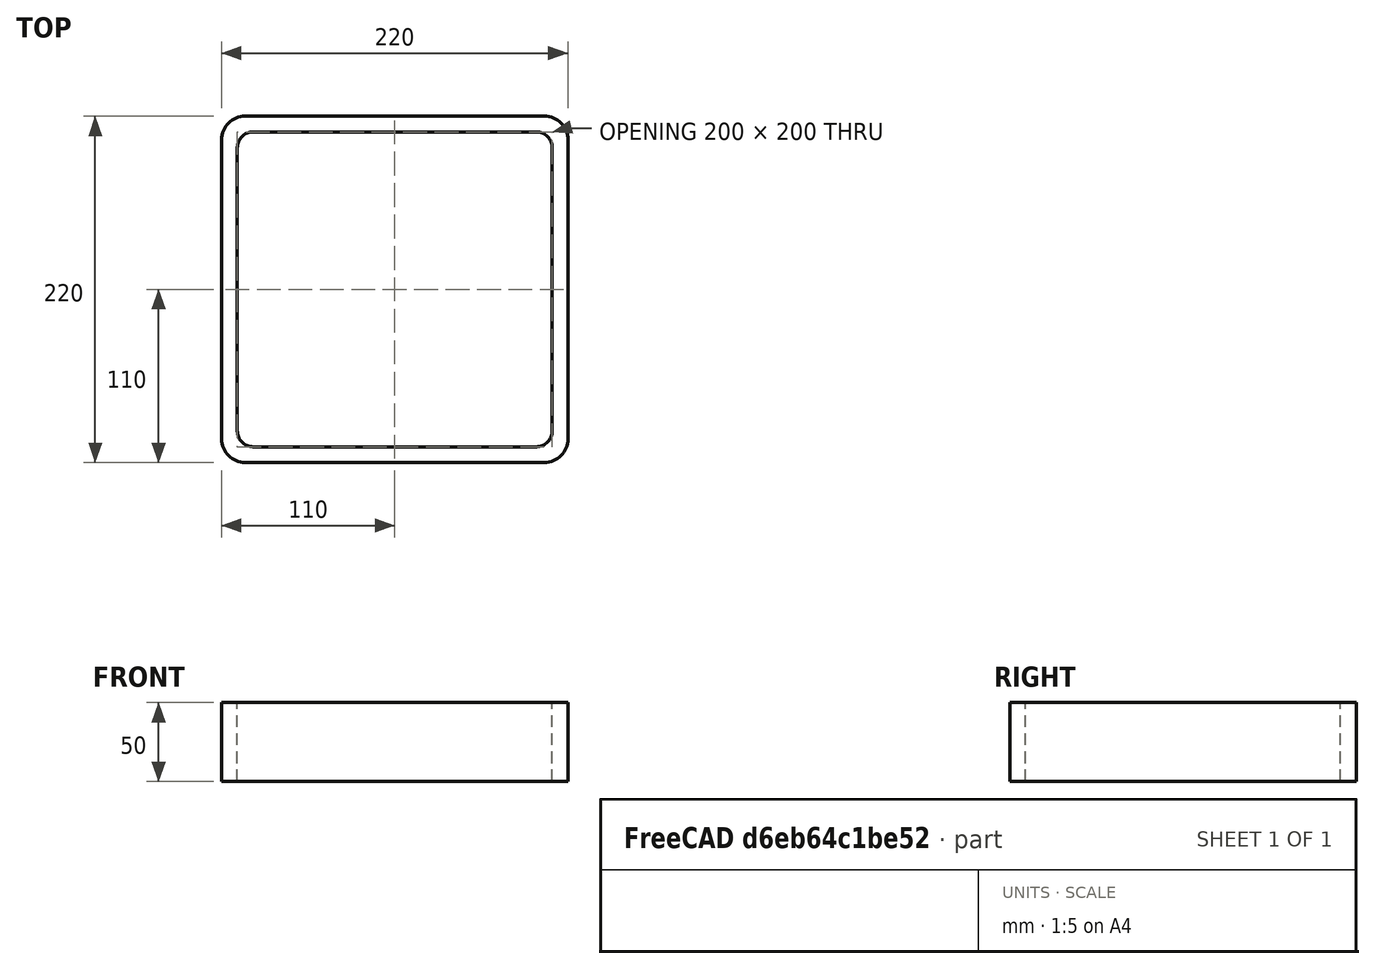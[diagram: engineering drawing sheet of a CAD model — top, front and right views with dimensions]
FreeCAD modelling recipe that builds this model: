
FCSTD DOCUMENT  (FreeCAD 0.15R4671 (Git))
Label: Square hollow section 220x220x10 EN10219 S235JRH
License: All rights reserved
LicenseURL: http://en.wikipedia.org/wiki/All_rights_reserved
objects: Sketcher::SketchObject×1, Part::Extrusion×1
note: 2 computed .brp shape members not serialized (recipe doc carries the construction recipe); baked Part::Feature solids carry a one-line shape summary decoded from their .brp

FEATURE [Sketcher::SketchObject] Sketch
  sketch-geometry (16):
    g0: LineSegment StartX=-90 StartY=100 StartZ=0 EndX=90 EndY=100 EndZ=0
    g1: LineSegment StartX=100 StartY=90 StartZ=0 EndX=100 EndY=-90 EndZ=0
    g2: LineSegment StartX=90 StartY=-100 StartZ=0 EndX=-90 EndY=-100 EndZ=0
    g3: LineSegment StartX=-100 StartY=-90 StartZ=0 EndX=-100 EndY=90 EndZ=0
    g4: LineSegment StartX=-95 StartY=110 StartZ=0 EndX=95 EndY=110 EndZ=0
    g5: LineSegment StartX=110 StartY=95 StartZ=0 EndX=110 EndY=-95 EndZ=0
    g6: LineSegment StartX=95 StartY=-110 StartZ=0 EndX=-95 EndY=-110 EndZ=0
    g7: LineSegment StartX=-110 StartY=-95 StartZ=0 EndX=-110 EndY=95 EndZ=0
    g8: ArcOfCircle CenterX=-90 CenterY=90 CenterZ=0 NormalX=0 NormalY=0 NormalZ=1 Radius=10 StartAngle=1.5708 EndAngle=3.14159
    g9: ArcOfCircle CenterX=90 CenterY=90 CenterZ=0 NormalX=0 NormalY=0 NormalZ=1 Radius=10 StartAngle=0 EndAngle=1.5708
    g10: ArcOfCircle CenterX=90 CenterY=-90 CenterZ=0 NormalX=0 NormalY=0 NormalZ=1 Radius=10 StartAngle=4.71239 EndAngle=6.28319
    g11: ArcOfCircle CenterX=-90 CenterY=-90 CenterZ=0 NormalX=0 NormalY=0 NormalZ=1 Radius=10 StartAngle=3.14159 EndAngle=4.71239
    g12: ArcOfCircle CenterX=95 CenterY=95 CenterZ=0 NormalX=0 NormalY=0 NormalZ=1 Radius=15 StartAngle=0 EndAngle=1.5708
    g13: ArcOfCircle CenterX=95 CenterY=-95 CenterZ=0 NormalX=0 NormalY=0 NormalZ=1 Radius=15 StartAngle=4.71239 EndAngle=6.28319
    g14: ArcOfCircle CenterX=-95 CenterY=-95 CenterZ=0 NormalX=0 NormalY=0 NormalZ=1 Radius=15 StartAngle=3.14159 EndAngle=4.71239
    g15: ArcOfCircle CenterX=-95 CenterY=95 CenterZ=0 NormalX=0 NormalY=0 NormalZ=1 Radius=15 StartAngle=1.5708 EndAngle=3.14159
  constraints (36):
    c: Horizontal(g2)
    c: Vertical(g3)
    c: Horizontal(g6)
    c: Vertical(g7)
    c: Tangent(g3,g8) = 1.5708
    c: Tangent(g0,g8) = 1.5708
    c: Tangent(g0,g9) = 1.5708
    c: Tangent(g1,g9) = 1.5708
    c: Tangent(g1,g10) = 1.5708
    c: Tangent(g2,g10) = 1.5708
    c: Tangent(g2,g11) = 1.5708
    c: Tangent(g3,g11) = 1.5708
    c: Tangent(g4,g12) = 1.5708
    c: Tangent(g5,g12) = 1.5708
    c: Tangent(g5,g13) = 1.5708
    c: Tangent(g6,g13) = 1.5708
    c: Tangent(g6,g14) = 1.5708
    c: Tangent(g7,g14) = 1.5708
    c: Tangent(g7,g15) = 1.5708
    c: Tangent(g4,g15) = 1.5708
    c: Equal(g9,g8)
    c: Equal(g9,g11)
    c: Equal(g9,g10)
    c: Equal(g12,g15)
    c: Equal(g12,g14)
    c: Equal(g12,g13)
    c: Symmetric(g4,g6,g-1)
    c: Symmetric(g7,g5,g-2)
    c: DistanceY(g4,g6) = -220
    c: DistanceX(g7,g5) = 220
    c: Symmetric(g3,g1,g-2)
    c: Symmetric(g0,g2,g-1)
    c: DistanceY(g0,g4) = 10
    c: DistanceX(g5,g1) = -10
    c: Radius(g9) = 10
    c: Radius(g12) = 15
FEATURE [Part::Extrusion] Extrude  label="Square hollow section 220x220x10 EN10219 S235JRH"
  Base = -> Sketch
  Dir = (0,0,50)
  Solid = true
